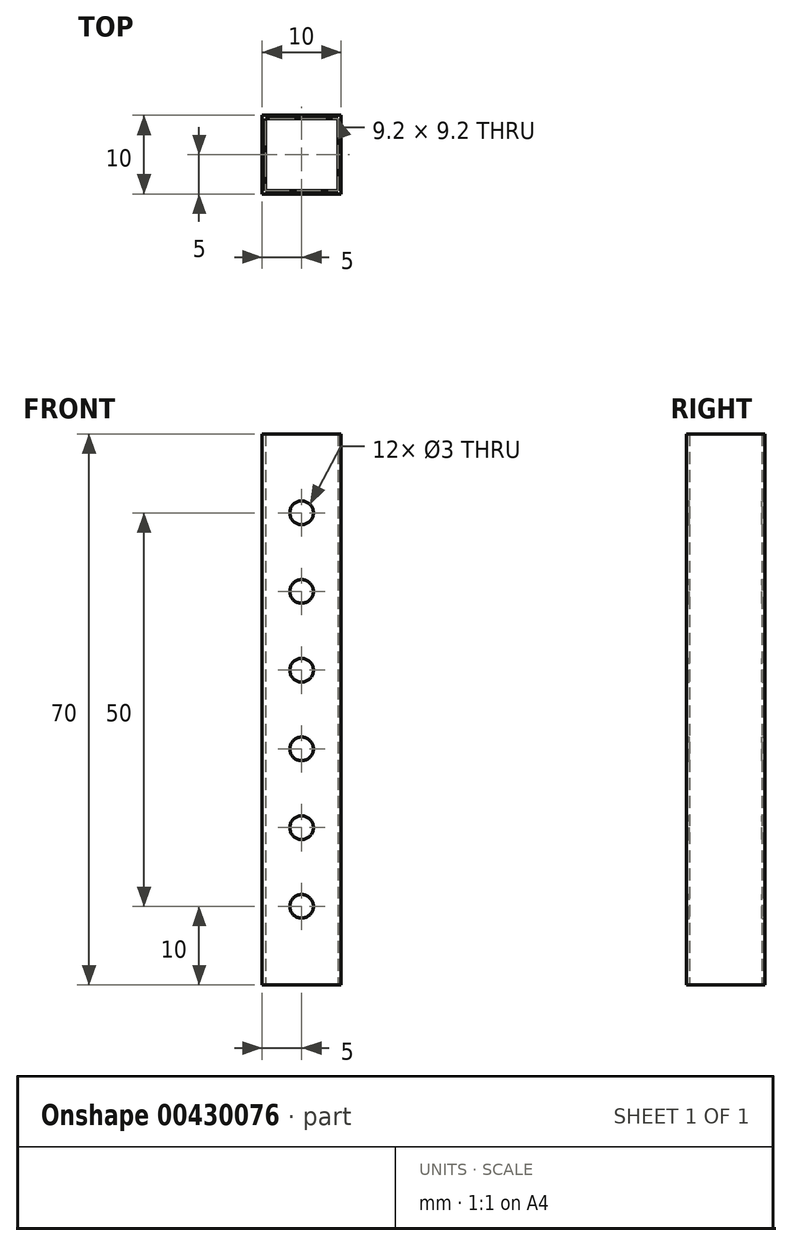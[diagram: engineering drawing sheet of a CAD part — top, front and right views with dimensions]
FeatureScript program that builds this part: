
annotation { "Feature Type Name" : "Feature", "Feature Type Description" : "" }
export const myFeature = defineFeature(function(context is Context, id is Id, definition is map)
    precondition{}
    {
        {
            var Q0;
            Q0=qCreatedBy(makeId("Top.planeOp"),FACE);
            var sketch = newSketch(context, id + "F0", { "sketchPlane" : qUnion([Q0])});
            skLineSegment(sketch, "E0.bottom", {"start": v(5, 5) * mm, "end": v(-5, 5) * mm});
            skLineSegment(sketch, "E0.top", {"start": v(5, -5) * mm, "end": v(-5, -5) * mm});
            skLineSegment(sketch, "E0.left", {"start": v(5, 5) * mm, "end": v(5, -5) * mm});
            skLineSegment(sketch, "E0.right", {"start": v(-5, 5) * mm, "end": v(-5, -5) * mm});
            skPoint(sketch, "E0.middle", {"position": v(0, 0) * mm});
            skLineSegment(sketch, "E1.bottom", {"start": v(4.6, 4.6) * mm, "end": v(-4.6, 4.6) * mm});
            skLineSegment(sketch, "E1.top", {"start": v(4.6, -4.6) * mm, "end": v(-4.6, -4.6) * mm});
            skLineSegment(sketch, "E1.left", {"start": v(4.6, 4.6) * mm, "end": v(4.6, -4.6) * mm});
            skLineSegment(sketch, "E1.right", {"start": v(-4.6, 4.6) * mm, "end": v(-4.6, -4.6) * mm});
            skSolve(sketch);
        }
        {
            var Q0;
            Q0=qSketchRegion(id+"F0",true);
            extrude(context, id + "F1", {"entities" : qUnion([Q0]), "depth" : (10 * 7) * mm});
        }
        {
            var Q0;
            Q0=makeQuery(id+"F1.opExtrude","SWEPT_FACE",FACE,{"disambiguationData":[OSD([sQuery(id+"F0.wireOp",EDGE,"E0.bottom")])]});
            var sketch = newSketch(context, id + "F2", { "sketchPlane" : qUnion([Q0])});
            skCircle(sketch, "E2", {"center": v(0, 60) * mm, "radius": 1.5 * mm});
            skCircle(sketch, "E3", {"center": v(0, 50) * mm, "radius": 1.5 * mm});
            skCircle(sketch, "E4", {"center": v(0, 40) * mm, "radius": 1.5 * mm});
            skCircle(sketch, "E5", {"center": v(0, 30) * mm, "radius": 1.5 * mm});
            skCircle(sketch, "E6", {"center": v(0, 20) * mm, "radius": 1.5 * mm});
            skCircle(sketch, "E7", {"center": v(0, 10) * mm, "radius": 1.5 * mm});
            skSolve(sketch);
        }
        {
            var Q0;
            Q0=makeQuery(id+"F2.imprint","IMPRINT",FACE,{"disambiguationData":[TD([[makeQuery(id+"F2.imprint","IMPRINT",EDGE,{"derivedFrom":sQuery(id+"F2.wireOp",EDGE,"E2")}),1.0]])]});
            var Q1;
            Q1=makeQuery(id+"F2.imprint","IMPRINT",FACE,{"disambiguationData":[TD([[makeQuery(id+"F2.imprint","IMPRINT",EDGE,{"derivedFrom":sQuery(id+"F2.wireOp",EDGE,"E3")}),1.0]])]});
            var Q2;
            Q2=makeQuery(id+"F2.imprint","IMPRINT",FACE,{"disambiguationData":[TD([[makeQuery(id+"F2.imprint","IMPRINT",EDGE,{"derivedFrom":sQuery(id+"F2.wireOp",EDGE,"E4")}),1.0]])]});
            var Q3;
            Q3=makeQuery(id+"F2.imprint","IMPRINT",FACE,{"disambiguationData":[TD([[makeQuery(id+"F2.imprint","IMPRINT",EDGE,{"derivedFrom":sQuery(id+"F2.wireOp",EDGE,"E5")}),1.0]])]});
            var Q4;
            Q4=makeQuery(id+"F2.imprint","IMPRINT",FACE,{"disambiguationData":[TD([[makeQuery(id+"F2.imprint","IMPRINT",EDGE,{"derivedFrom":sQuery(id+"F2.wireOp",EDGE,"E6")}),1.0]])]});
            var Q5;
            Q5=makeQuery(id+"F2.imprint","IMPRINT",FACE,{"disambiguationData":[TD([[makeQuery(id+"F2.imprint","IMPRINT",EDGE,{"derivedFrom":sQuery(id+"F2.wireOp",EDGE,"E7")}),1.0]])]});
            extrude(context, id + "F3", {"entities" : qUnion([Q0, Q1, Q2, Q3, Q4, Q5]), "operationType" : NewBodyOperationType.REMOVE, "oppositeDirection" : true, "depth" : 25 * mm});
        }
    });
